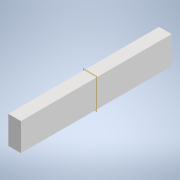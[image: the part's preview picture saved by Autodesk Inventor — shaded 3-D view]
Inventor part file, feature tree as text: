
AUTODESK INVENTOR PART (.ipt)
format: ipt  version: 2022.1 (Build 261234020, 234B)  size: 96,256 bytes
history: native  units: in
note: dims shown in document units (in); Inventor stores cm internally (conversion verified against a paired STEP export)
features: extrude x1, sketch x1
ambient origin geometry x8: Origin, YZ Plane, XZ Plane, XY Plane, X Axis, Y Axis, Z Axis, Center Point
bodies: Solid1 (feature_tree)
feature tree (2):
  extrude  "Extrusion1"  Depth=1.5in
  sketch  "Sketch1"  dims[d0=3.315in d1=1.5in d2=18.0in d3=0.0in]
